# Revit family: VRSE-5-48
name_source: partatom
category: Lighting Fixtures
units: mm (PartAtom-declared; Revit-internal decimal feet)

## family parameters
Always vertical = Yes
Cut with Voids When Loaded = No
Host = Floor
Light Source = Yes
OmniClass Number = 23.80.70.11.14.17
OmniClass Title = Direct/Indirect
Part Type = Normal
Room Calculation Point = No
Round Connector Dimension = Use Diameter
Shared = No

## types (2) — shared parameters
Assembly Code = D5020200
Color Filter = 16777215
Description = LED Vandal Resistant Surface
Dimming Lamp Color Temperature Shift = <None>
Emit Shape Visible in Rendering = No
Emit from Rectangle Length = 3' - 11"
Emit from Rectangle Width = 0' - 9 1/4"
Housing Finish = Extruded Aluminum - Viscor - White
LED Tray Finish = Metal - Viscor - White
Lamp = LED
Length = 3' - 11"
Lens Finish = Polycarbonate - Viscor - Frosted
Manufacturer = CERTOLUX by VISCOR
Model = VRSE-5
Tilt Angle = -90.00°
URL = https://www.viscor.com
Voltage = 120 V
Width = 0' - 5 5/16"

## per-type parameters (varying)
| type | Apparent Load | Lamp Wattage | Photometric Web File |
| VRSE5-48-LED840K035LUNV-P55 | 26 VA | 26 VA | VRSE-5-48-LED840K035LUNV-P55.ies |
| VRSE5-48-LED840K055LUNV-P55 | 43 VA | 43 VA | VRSE-5-48-LED840K055LUNV-P55.ies |

## geometry (parser evidence)
native form markers: Sweep x3
no freeform markers — native parametric forms only
